# Revit family: WC Sustenta
name_source: partatom
category: Aparatos sanitarios
units: mm (PartAtom-declared; Revit-internal decimal feet)

## family parameters
Activar corte en vistas = No
Compartido = No
Corte con vacíos al cargar = No
Cota de conector redondo = Usar diámetro
Mantener orientación de anotación = No
Número OmniClass = 23.45.00.00
Punto de cálculo de habitación = No
Se basa en plano de trabajo = No
Siempre vertical = Sí
Tipo de pieza = Normal
Título OmniClass = Sanitary, Laundry, and Cleaning Equipment

## types (1)
- WC Sustenta
    Arrastre = 12,2 m. mínimo
    Comentarios de tipo = Ceramic
    Componentes Incluídos = Kit de fijación al piso y cubre pijas.
Kit de sujeción y acoplamiento para el tanque.
    Cumplimiento = NOM-002-CONAGUA-2021
    Desalojo = 350 gr. mínimo.
    Descripción = Inodoro ecológico elongado para espacios
reducidos de trampa expuesta, taza y tanque.
Diseño ergonómico de construcción robusta,
tecnología con sistema vórtice, espejo de agua
óptimo y con trampa esmaltada.
Inodoro libre de alabeo.
    Elevación por defecto = 0"
    Fabricante = HELVEX
    High Gloss Ceramic = High Gloss Ceramic
    Imagen de tipo = <Ninguno>
    Inlet Threads = CONEXIÓN:
A la alimentación Ø1/2" - 14 NPSM.
A la descarga se acopla al Ø del drenaje de 4" con
brida sanitaria o cuello de cera.
    Material = Cerámica porcelanizada de alto brillo.
Calidad "A".
    Max. Working Pressure = 85.3 psi
    Maximum Consumption = 0.66 gpf
    Min. Working Pressure = 3.6 psi
    Modelo = WC Sustenta
    Operación = Presione el botón un segundo para una descarga
ecológica.
    Rango de gasto = 2,5 LPD ± 10%
    Total Height = 32"
    Total Length = 28"
    Total Width = 13"
    Válvulas = Válvula de admisión silenciosa.
Válvulas calibradas.
Válvula de descarga con sello hermético.
Válvula de descarga de Ø 2" tipo torre.

## geometry (parser evidence)
native form markers: Sweep x3
no freeform markers — native parametric forms only
